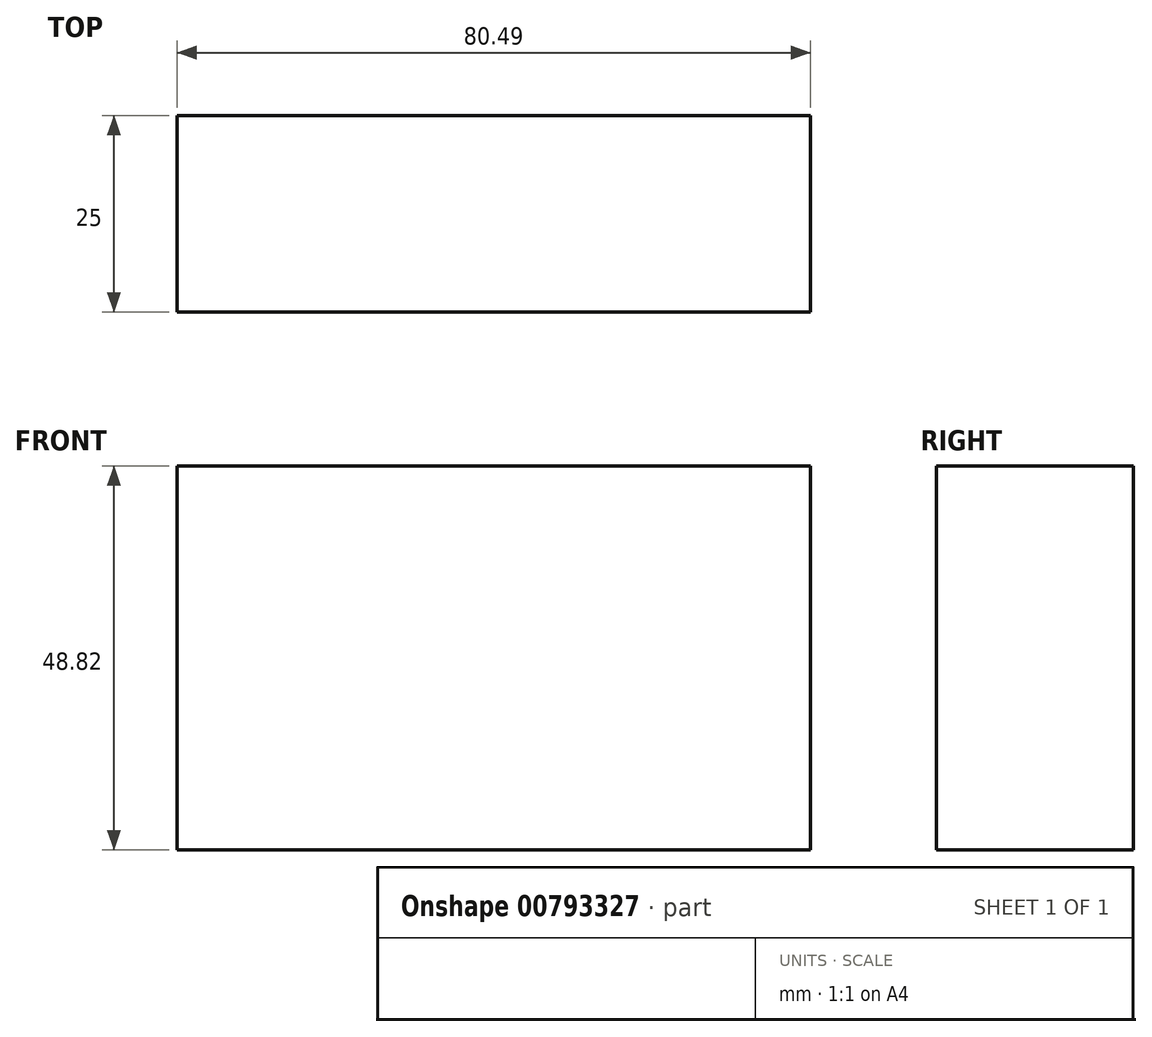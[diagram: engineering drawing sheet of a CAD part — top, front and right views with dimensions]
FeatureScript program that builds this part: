
annotation { "Feature Type Name" : "Feature", "Feature Type Description" : "" }
export const myFeature = defineFeature(function(context is Context, id is Id, definition is map)
    precondition{}
    {
        {
            var Q0;
            Q0=qCreatedBy(makeId("Front.planeOp"),FACE);
            var sketch = newSketch(context, id + "F0", { "sketchPlane" : qUnion([Q0])});
            skLineSegment(sketch, "E0.bottom", {"start": v(-138.75, 28.6) * mm, "end": v(-58.26, 28.6) * mm});
            skLineSegment(sketch, "E0.top", {"start": v(-138.75, -20.23) * mm, "end": v(-58.26, -20.23) * mm});
            skLineSegment(sketch, "E0.left", {"start": v(-138.75, 28.6) * mm, "end": v(-138.75, -20.23) * mm});
            skLineSegment(sketch, "E0.right", {"start": v(-58.26, 28.6) * mm, "end": v(-58.26, -20.23) * mm});
            skSolve(sketch);
        }
        {
            var Q0;
            Q0 = qSketchRegion(id + "F0", true);
            extrude(context, id + "F1", {"entities" : qUnion([Q0]), "depth" : 25 * mm, "offsetDistance" : 25 * mm});
        }
    });
